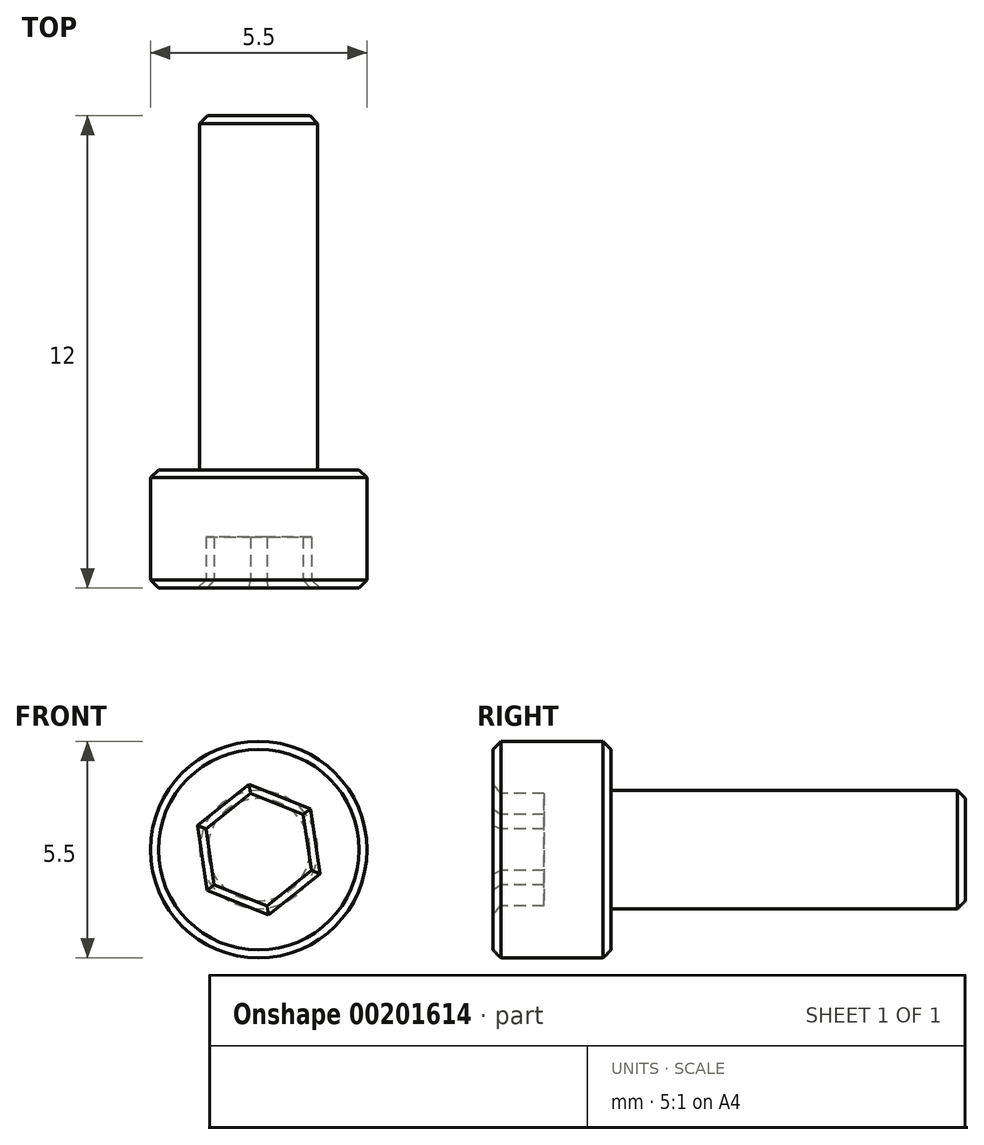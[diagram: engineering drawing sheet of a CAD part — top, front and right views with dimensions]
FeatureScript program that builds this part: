
annotation { "Feature Type Name" : "Feature", "Feature Type Description" : "" }
export const myFeature = defineFeature(function(context is Context, id is Id, definition is map)
    precondition{}
    {
        {
            var Q0;
            Q0=qCreatedBy(makeId("Front.planeOp"),FACE);
            var sketch = newSketch(context, id + "F0", { "sketchPlane" : qUnion([Q0])});
            skCircle(sketch, "E0", {"center": v(0, 0) * mm, "radius": 1.5 * mm});
            skSolve(sketch);
        }
        {
            var Q0;
            Q0=makeQuery(id+"F0.imprint","IMPRINT",FACE,{"disambiguationData":[TD([[makeQuery(id+"F0.imprint","IMPRINT",EDGE,{"derivedFrom":sQuery(id+"F0.wireOp",EDGE,"E0")}),1.0]])]});
            extrude(context, id + "F1", {"entities" : qUnion([Q0]), "depth" : 9 * mm});
        }
        {
            var Q0;
            Q0=makeQuery(id+"F1.opExtrude","CAP_FACE",FACE,{"disambiguationData":[OSD([sQuery(id+"F0.wireOp",EDGE,"E0")])],"isStart":false});
            var sketch = newSketch(context, id + "F2", { "sketchPlane" : qUnion([Q0])});
            skCircle(sketch, "E1", {"center": v(0, 0) * mm, "radius": 2.75 * mm});
            skSolve(sketch);
        }
        {
            var Q0;
            Q0 = qSketchRegion(id + "F2", true);
            extrude(context, id + "F3", {"entities" : qUnion([Q0]), "operationType" : NewBodyOperationType.ADD, "depth" : 3 * mm});
        }
        {
            var Q0;
            Q0=makeQuery(id+"F3.opExtrude","CAP_FACE",FACE,{"disambiguationData":[OSD([sQuery(id+"F2.wireOp",EDGE,"E1")])],"isStart":false});
            var sketch = newSketch(context, id + "F4", { "sketchPlane" : qUnion([Q0])});
            skCircle(sketch, "E2.cCircle", {"center": v(0, 0) * mm, "radius": 1.25 * mm, "construction": true});
            skLineSegment(sketch, "E2.0", {"start": v(1.34, -0.53) * mm, "end": v(0.21, -1.43) * mm});
            skLineSegment(sketch, "E2.1", {"start": v(0.21, -1.43) * mm, "end": v(-1.13, -0.9) * mm});
            skLineSegment(sketch, "E2.2", {"start": v(-1.13, -0.9) * mm, "end": v(-1.34, 0.53) * mm});
            skLineSegment(sketch, "E2.3", {"start": v(-1.34, 0.53) * mm, "end": v(-0.21, 1.43) * mm});
            skLineSegment(sketch, "E2.4", {"start": v(-0.21, 1.43) * mm, "end": v(1.13, 0.9) * mm});
            skLineSegment(sketch, "E2.5", {"start": v(1.13, 0.9) * mm, "end": v(1.34, -0.53) * mm});
            skPoint(sketch, "E2.0.midPoint", {"position": v(0.78, -0.98) * mm});
            skSolve(sketch);
        }
        {
            var Q0;
            Q0=makeQuery(id+"F4.imprint","IMPRINT",FACE,{"disambiguationData":[TD([[makeQuery(id+"F4.imprint","IMPRINT",EDGE,{"derivedFrom":sQuery(id+"F4.wireOp",EDGE,"E2.0")}),-1.0]])]});
            extrude(context, id + "F5", {"entities" : qUnion([Q0]), "operationType" : NewBodyOperationType.REMOVE, "oppositeDirection" : true, "depth" : 1.3 * mm});
        }
        {
            var Q0;
            Q0=makeQuery(id+"F3.opExtrude","CAP_EDGE",EDGE,{"disambiguationData":[OSD([sQuery(id+"F2.wireOp",EDGE,"E1")])],"isStart":false});
            var Q1;
            Q1=makeQuery(id+"F3.opExtrude","CAP_EDGE",EDGE,{"disambiguationData":[OSD([sQuery(id+"F2.wireOp",EDGE,"E1")])],"isStart":true});
            var Q2;
            Q2=makeQuery(id+"F1.opExtrude","CAP_EDGE",EDGE,{"disambiguationData":[OSD([sQuery(id+"F0.wireOp",EDGE,"E0")])],"isStart":true});
            var Q3;
            Q3=makeQuery(id+"F3.opExtrude","CAP_FACE",FACE,{"disambiguationData":[OSD([sQuery(id+"F2.wireOp",EDGE,"E1")])],"isStart":false});
            chamfer(context, id + "F6", {"entities" : qUnion([Q0, Q1, Q2, Q3]), "width" : .2 * mm, "tangentPropagation" : true});
        }
    });
